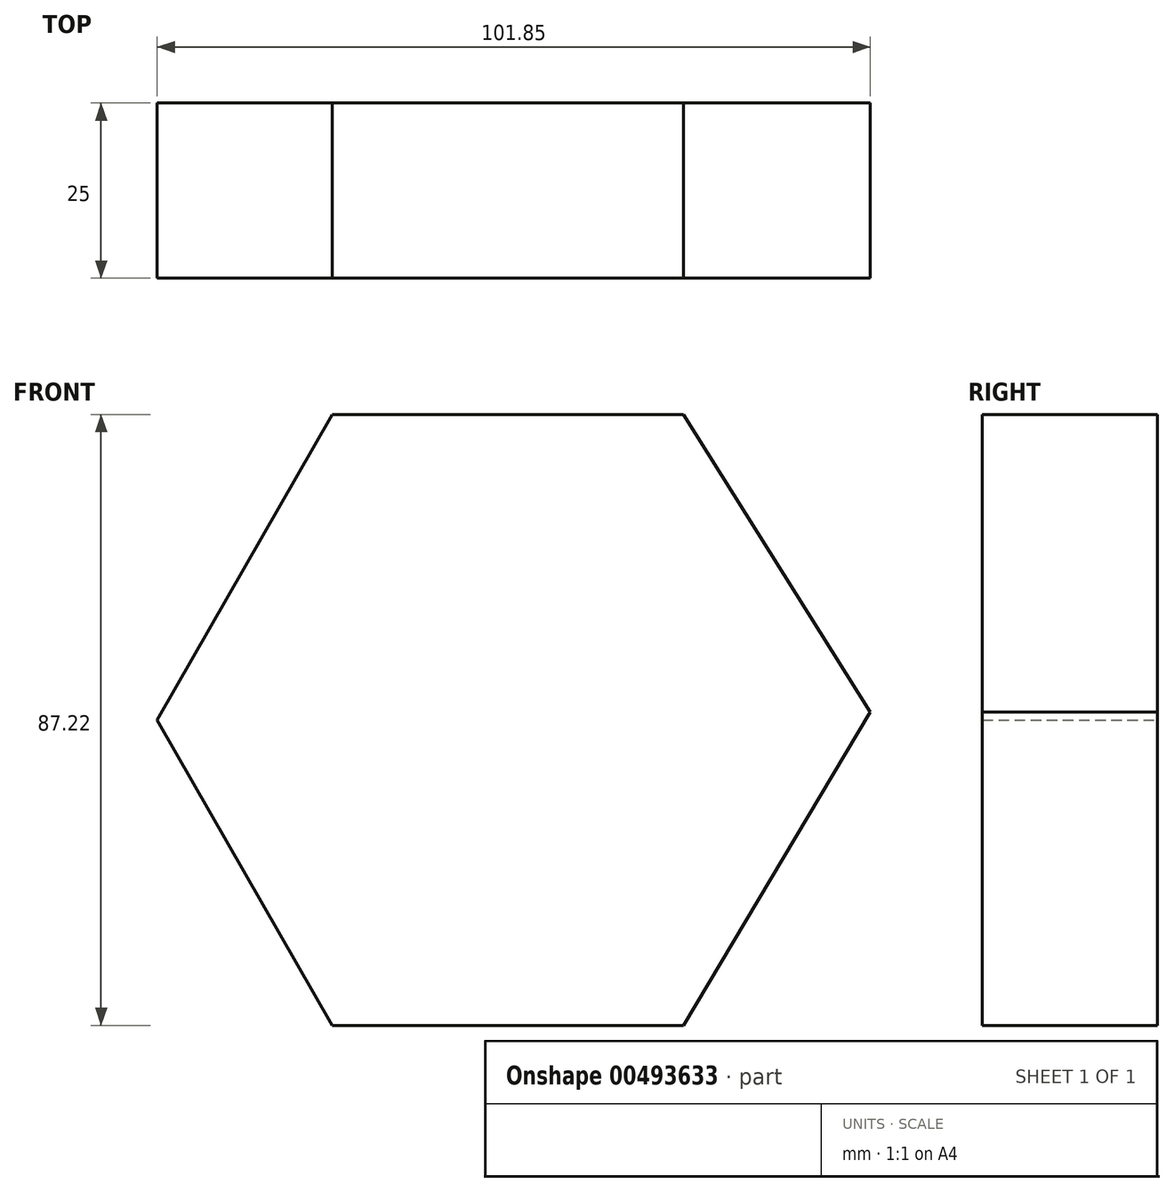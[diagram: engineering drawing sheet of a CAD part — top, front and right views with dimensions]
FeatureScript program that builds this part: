
annotation { "Feature Type Name" : "Feature", "Feature Type Description" : "" }
export const myFeature = defineFeature(function(context is Context, id is Id, definition is map)
    precondition{}
    {
        {
            var Q0;
            Q0=qCreatedBy(makeId("Front.planeOp"),FACE);
            var sketch = newSketch(context, id + "F0", { "sketchPlane" : qUnion([Q0])});
            skLineSegment(sketch, "E0", {"start": v(-24.96, 40.3) * mm, "end": v(25.25, 40.3) * mm});
            skLineSegment(sketch, "E1", {"start": v(25.25, 40.3) * mm, "end": v(51.93, -2.15) * mm});
            skLineSegment(sketch, "E2", {"start": v(-24.96, 40.3) * mm, "end": v(-49.92, -3.3) * mm});
            skLineSegment(sketch, "E3", {"start": v(-49.92, -3.3) * mm, "end": v(-24.96, -46.9) * mm});
            skLineSegment(sketch, "E4", {"start": v(-24.96, -46.9) * mm, "end": v(25.25, -46.9) * mm});
            skLineSegment(sketch, "E5", {"start": v(25.25, -46.9) * mm, "end": v(51.93, -2.15) * mm});
            skSolve(sketch);
        }
        {
            var Q0;
            Q0 = qSketchRegion(id + "F0", true);
            extrude(context, id + "F1", {"entities" : qUnion([Q0]), "depth" : 25 * mm});
        }
    });
